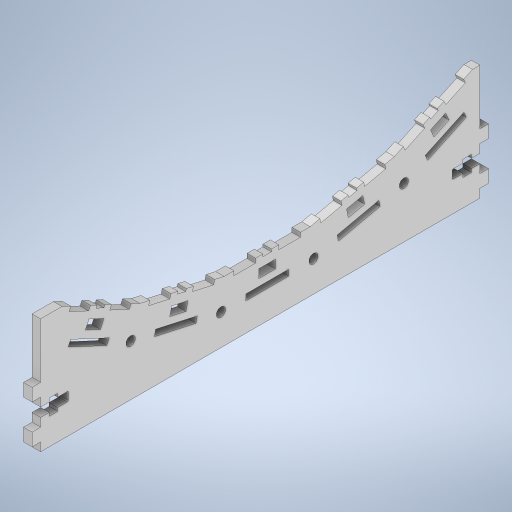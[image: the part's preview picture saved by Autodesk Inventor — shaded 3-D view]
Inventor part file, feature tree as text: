
AUTODESK INVENTOR PART (.ipt)
format: ipt  version: 2024.1 (Build 281209000, 209)  size: 2,624,512 bytes
history: native  units: mm
features: other x20, extrude x4, sketch x2
ambient origin geometry x8: Origin, YZ Plane, XZ Plane, XY Plane, X Axis, Y Axis, Z Axis, Center Point
bodies: Body1 (feature_tree)
feature tree (26):
  other  "Table"
  other  "shared_parameters.ipt"
  other  "Numéro de pièce = switchplate-support-01"
  other  "Numéro de pièce = switchplate-support-02"
  other  "Numéro de pièce = switchplate-support-03"
  other  "Numéro de pièce = switchplate-support-04"
  other  "Numéro de pièce = switchplate-support-05"
  other  "Numéro de pièce = switchplate-support-06"
  other  "Blocs"
  sketch  "Sketch1"  dims[d27=2.0mm d28=0.0mm d153=0.0mm d154=0.0mm]
  extrude  "Base"  TaperAngle=0.0deg  [1 undecoded]
  extrude  "Standard anchors"  TaperAngle=0.0deg  [1 undecoded]
  extrude  "No back screw hole"  TaperAngle=0.0deg  [1 undecoded]
  extrude  "Short plate"  Depth=2.0mm
  sketch  "Sketch2"  dims[d193=27.0mm d196=0.0mm d197=0.0mm d201=0.0mm d202=0.0mm d203=2.0mm d207=0.0mm d208=0.0mm d232=20.454483mm d257=7.0mm d263=10.0mm d3=2.0mm d7=6.1mm d10=2.0mm d11=2.0mm d12=0.8mm d13=2.0mm d14=0.8mm d15=2.1mm d18=2.0mm d19=0.8mm d20=0.8mm d21=2.5mm d22=2.5mm d23=2.1mm d29=2.0mm d34=2.0mm d35=2.0mm d36=2.0mm d37=2.0mm d38=2.0mm d39=0.25mm d264=10.0mm d43=1.0mm d48=17.0mm d120=3.0mm d124=0.7mm d125=0.7mm d126=1.0mm d128=1.0mm d137=1.0mm d127=5.07mm d129=1.73mm d131=0.55mm d132=2.0mm d133=0.55mm d135=1.73mm d136=5.07mm d138=3.9mm d139=2.0mm d140=1.5mm d141=1.4mm d142=10.0mm d143=5.1mm d272=11.34464mm d273=17.889625mm d274=90.0deg d275=13.526302mm d276=11.34464mm d277=2.2mm d278=5.886189mm d279=5.886189mm d280=2.2mm d281=5.886189mm d282=5.886189mm d283=2.2mm d284=2.2mm]
  other  "Anchor (screw side)"
  other  "Anchor (nut side)"
  other  "Switch support"
  other  "Switch support:1"
  other  "Switch support:2"
  other  "Switch support:3"
  other  "Switch support:4"
  other  "Switch support:5"
  other  "Anchor (nut side):1"
  other  "Anchor (nut side):2"
  other  "Anchor (nut side):3"
note: 3 required parameter values undecoded (feature->parameter linkage not recoverable at this tier; creation-order binding heuristic only, values carry confidence <= 0.55)
